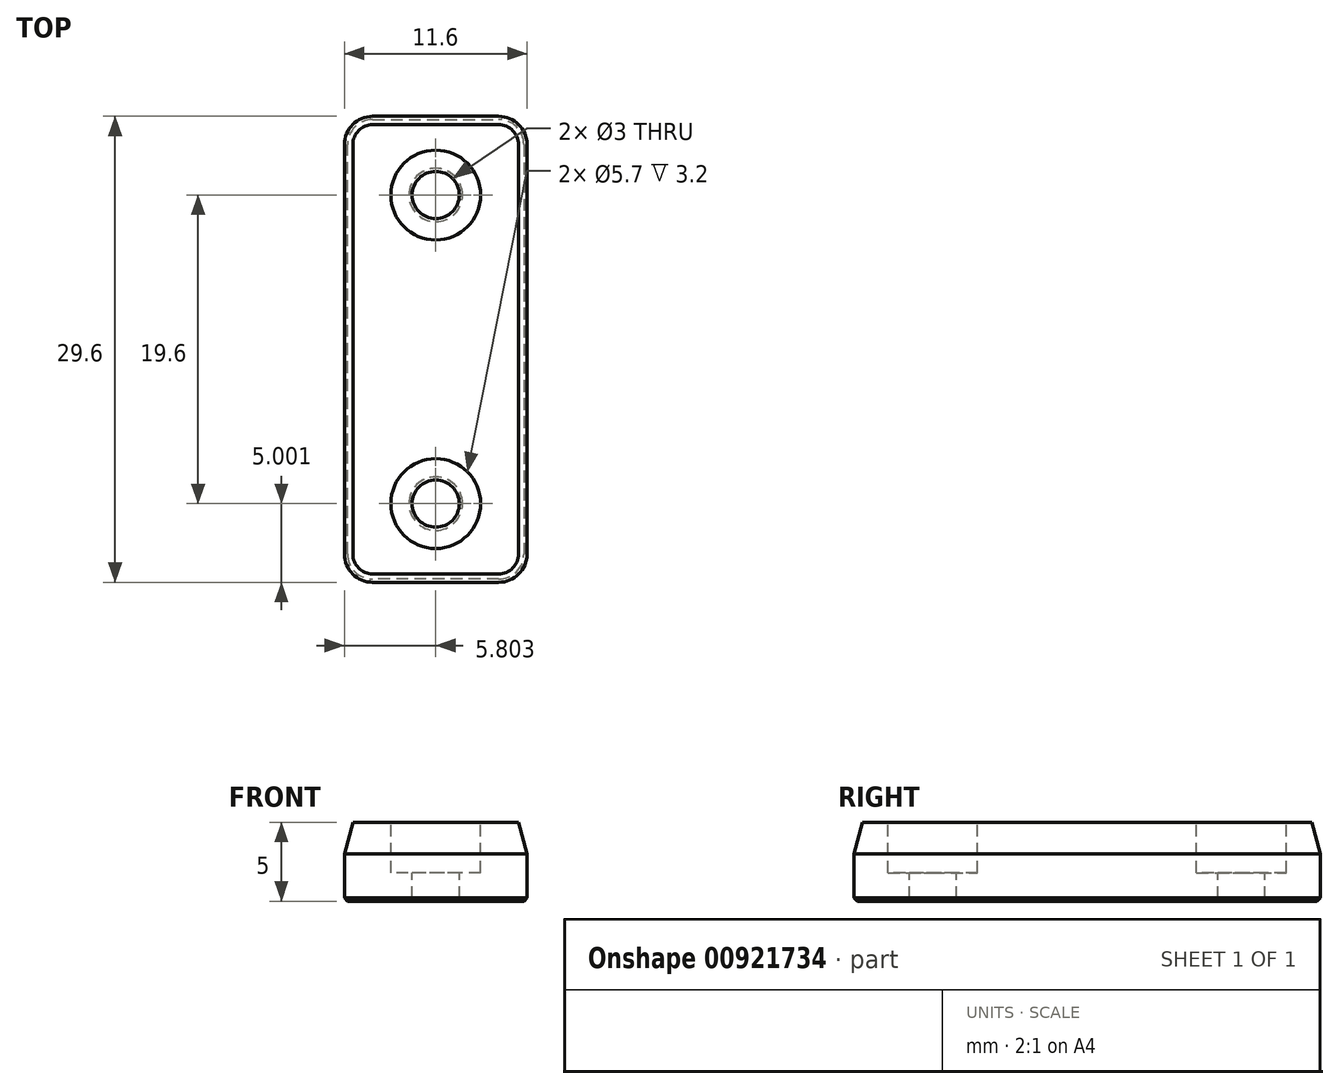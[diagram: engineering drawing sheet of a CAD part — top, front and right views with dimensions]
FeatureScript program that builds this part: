
annotation { "Feature Type Name" : "Feature", "Feature Type Description" : "" }
export const myFeature = defineFeature(function(context is Context, id is Id, definition is map)
    precondition{}
    {
        {
            var Q0;
            Q0=qCreatedBy(makeId("Top.planeOp"),FACE);
            var sketch = newSketch(context, id + "F0", { "sketchPlane" : qUnion([Q0])});
            skLineSegment(sketch, "E0.0", {"start": v(-34.48, 68.68) * mm, "end": v(-34.48, 42.68) * mm});
            skLineSegment(sketch, "E0.1", {"start": v(-44.28, 70.48) * mm, "end": v(-36.28, 70.48) * mm});
            skLineSegment(sketch, "E0.2", {"start": v(-46.08, 68.68) * mm, "end": v(-46.08, 42.68) * mm});
            skLineSegment(sketch, "E0.3", {"start": v(-44.28, 40.88) * mm, "end": v(-36.28, 40.88) * mm});
            skArc(sketch, "E1.filletArc", {"start": v(-44.28, 70.48) * mm, "mid": v(-45.55, 69.95) * mm, "end": v(-46.08, 68.68) * mm});
            skArc(sketch, "E2.filletArc", {"start": v(-34.48, 68.68) * mm, "mid": v(-35, 69.95) * mm, "end": v(-36.28, 70.48) * mm});
            skArc(sketch, "E3.filletArc", {"start": v(-36.28, 40.88) * mm, "mid": v(-35, 41.4) * mm, "end": v(-34.48, 42.68) * mm});
            skArc(sketch, "E4.filletArc", {"start": v(-46.08, 42.68) * mm, "mid": v(-45.55, 41.4) * mm, "end": v(-44.28, 40.88) * mm});
            skSolve(sketch);
        }
        {
            var Q0;
            Q0 = qSketchRegion(id + "F0", true);
            extrude(context, id + "F1", {"entities" : qUnion([Q0]), "depth" : 5 * mm, "offsetDistance" : 25 * mm});
        }
        {
            var Q0;
            Q0=makeQuery(id+"F1.opExtrude","CAP_FACE",FACE,{"disambiguationData":[OSD([sQuery(id+"F0.wireOp",EDGE,"E0.0"),sQuery(id+"F0.wireOp",EDGE,"E0.1"),sQuery(id+"F0.wireOp",EDGE,"E0.2"),sQuery(id+"F0.wireOp",EDGE,"E0.3"),sQuery(id+"F0.wireOp",EDGE,"E1.filletArc"),sQuery(id+"F0.wireOp",EDGE,"E2.filletArc"),sQuery(id+"F0.wireOp",EDGE,"E3.filletArc"),sQuery(id+"F0.wireOp",EDGE,"E4.filletArc")])],"isStart":false});
            var sketch = newSketch(context, id + "F2", { "sketchPlane" : qUnion([Q0])});
            skLineSegment(sketch, "E5", {"start": v(-40.28, 70.48) * mm, "end": v(-40.28, 65.48) * mm});
            skLineSegment(sketch, "E6", {"start": v(-40.28, 40.88) * mm, "end": v(-40.28, 45.88) * mm});
            skCircle(sketch, "E7", {"center": v(-40.28, 65.48) * mm, "radius": 1.5 * mm});
            skCircle(sketch, "E8", {"center": v(-40.28, 45.88) * mm, "radius": 1.5 * mm});
            skCircle(sketch, "E9", {"center": v(-40.28, 65.48) * mm, "radius": 2.85 * mm});
            skCircle(sketch, "E10", {"center": v(-40.28, 45.88) * mm, "radius": 2.85 * mm});
            skSolve(sketch);
        }
        {
            var Q0;
            Q0=makeQuery(id+"F2.imprint","IMPRINT",FACE,{"disambiguationData":[TD([[makeQuery(id+"F2.imprint","IMPRINT",EDGE,{"derivedFrom":sQuery(id+"F2.wireOp",EDGE,"E7")}),1.0]])]});
            var Q1;
            Q1=makeQuery(id+"F2.imprint","IMPRINT",FACE,{"disambiguationData":[TD([[makeQuery(id+"F2.imprint","IMPRINT",EDGE,{"derivedFrom":sQuery(id+"F2.wireOp",EDGE,"E8")}),1.0]])]});
            extrude(context, id + "F3", {"entities" : qUnion([Q0, Q1]), "operationType" : NewBodyOperationType.REMOVE, "oppositeDirection" : true, "depth" : 25 * mm, "offsetDistance" : 25 * mm});
        }
        {
            var Q0;
            Q0=makeQuery(id+"F2.imprint","IMPRINT",FACE,{"disambiguationData":[TD([[makeQuery(id+"F2.imprint","IMPRINT",EDGE,{"derivedFrom":sQuery(id+"F2.wireOp",EDGE,"E7")}),-1.0]])]});
            var Q1;
            Q1=makeQuery(id+"F2.imprint","IMPRINT",FACE,{"disambiguationData":[TD([[makeQuery(id+"F2.imprint","IMPRINT",EDGE,{"derivedFrom":sQuery(id+"F2.wireOp",EDGE,"E8")}),-1.0]])]});
            extrude(context, id + "F4", {"entities" : qUnion([Q0, Q1]), "operationType" : NewBodyOperationType.REMOVE, "oppositeDirection" : true, "depth" : 3.2 * mm, "offsetDistance" : 25 * mm});
        }
        {
            var Q0;
            Q0=makeQuery(id+"F4.boolean.opBoolean","COPY",EDGE,{"derivedFrom":makeQuery(id+"F4.opExtrude","CAP_EDGE",EDGE,{"disambiguationData":[OSD([sQuery(id+"F2.wireOp",EDGE,"E7")])],"isStart":false})});
            var Q1;
            Q1=makeQuery(id+"F4.boolean.opBoolean","COPY",EDGE,{"derivedFrom":makeQuery(id+"F4.opExtrude","CAP_EDGE",EDGE,{"disambiguationData":[OSD([sQuery(id+"F2.wireOp",EDGE,"E8")])],"isStart":false})});
            var Q2;
            Q2=makeQuery(id+"F1.opExtrude","CAP_FACE",FACE,{"disambiguationData":[OSD([sQuery(id+"F0.wireOp",EDGE,"E0.0"),sQuery(id+"F0.wireOp",EDGE,"E0.1"),sQuery(id+"F0.wireOp",EDGE,"E0.2"),sQuery(id+"F0.wireOp",EDGE,"E0.3"),sQuery(id+"F0.wireOp",EDGE,"E1.filletArc"),sQuery(id+"F0.wireOp",EDGE,"E2.filletArc"),sQuery(id+"F0.wireOp",EDGE,"E3.filletArc"),sQuery(id+"F0.wireOp",EDGE,"E4.filletArc")])],"isStart":true});
            var Q3;
            Q3=makeQuery(id+"F4.boolean.opBoolean","COPY",EDGE,{"derivedFrom":makeQuery(id+"F4.opExtrude","CAP_EDGE",EDGE,{"disambiguationData":[OSD([sQuery(id+"F2.wireOp",EDGE,"E9")])],"isStart":true})});
            var Q4;
            Q4=makeQuery(id+"F4.boolean.opBoolean","COPY",EDGE,{"derivedFrom":makeQuery(id+"F4.opExtrude","CAP_EDGE",EDGE,{"disambiguationData":[OSD([sQuery(id+"F2.wireOp",EDGE,"E10")])],"isStart":true})});
            chamfer(context, id + "F5", {"entities" : qUnion([Q0, Q1, Q2, Q3, Q4]), "width" : 0.2 * mm, "tangentPropagation" : true});
        }
        {
            var Q0;
            Q0=makeQuery(id+"F1.opExtrude","CAP_EDGE",EDGE,{"disambiguationData":[OSD([sQuery(id+"F0.wireOp",EDGE,"E0.0")])],"isStart":false});
            chamfer(context, id + "F6", {"entities" : qUnion([Q0]), "chamferType" : ChamferType.OFFSET_ANGLE, "width" : 2 * mm, "oppositeDirection" : false, "angle" : 15 * degree, "tangentPropagation" : true});
        }
    });
